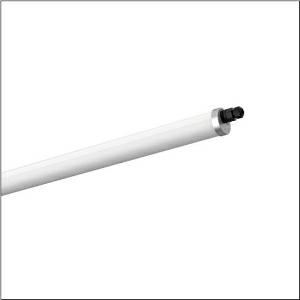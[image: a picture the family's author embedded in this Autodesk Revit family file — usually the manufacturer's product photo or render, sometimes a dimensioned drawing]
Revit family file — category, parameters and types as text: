
# Revit family: monsun_r__31_tube_51ft10dn4a0a_ff33
name_source: partatom
category: Lighting Fixtures
units: mm (PartAtom-declared; Revit-internal decimal feet)

## family parameters
Cut with Voids When Loaded = No
Host = Face
Light Source = No
Part Type = Normal
Room Calculation Point = No
Round Connector Dimension = Use Diameter
Shared = No

## types (1)
- Monsun® 31 Tube (1 x LED, 10000 lm, 58 W, 4000K)
    Apparent Load = 58 VA
    CIE Flux Codes = 42 71 90 91 100
    Color Rendering = 80
    Color Temperature = 4000K
    Default Elevation = 1800 mm
    Description = Monsun® 31 Tube, tubular luminaire, primary optical cover: diffuser, of PMMA, light emission: direct distribution, primary light characteristic: symmetric, installation type: suspended mounting, surface-mounted, LED, rated luminous flux: 10.000lm, luminous efficacy: 160lm/W, light colour: 840, colour temperature: 4000K, control gear: DALI 2, with with 1 terminal, 5-pole, max. 2.5mm², through-wiring: 5x 1.5mm², mains connection: 220..240V, AC, 50/60Hz, rated input power: 58W, housing, cylindrical, of PMMA, semi-transparent, matt white, with luminaire and ceiling fastening, V4A, mounting with brackets of stainless steel, length: 1.570mm, diameter: 75mm, end cap, of stainless steel (V4A), protection rating (complete): IP67/IP69K, insulation class (complete): insulation class I (protective earthing), certification: CE, UKCA, impact resistance: IK07, permissible operating ambient temperature: -20..+40°C, corresponds to IFS (International Featured Standards) requirements for safety and quality in the food industry, usage in unprotected outdoor areas possible with horizontal mounting, contact your sales advisor before using the luminaires in applications with unclear chemical exposure, large temperature fluctuations or condensation-forming humidity, packaging unit: 1 piece
    Height = 83 mm
    Lamp = 1 x LED
    Lamp Light Flux = 10000 lm
    Lamp Power = 58 W
    Lamp count = 1
    Length = 1570 mm
    Luminous efficacy = 172 lm/W
    Manufacturer = Siteco
    ModVariant = No
    Model = 51FT10DN4A0A
    Mounting Place = Ceiling
    Mounting Type = Pendant
    Number of Poles = 1
    OnlyDefault = Yes
    Power Factor = 1
    Product Name = Monsun® 31 Tube
    Product group = tubular luminaire
    ProductGroupID = 906
    Protection Class = Protection class I
    RLX_Detail_Level = 1
    RLX_Emergency_Light_Flux = 0 lm
    RLX_Emergency_Type = 0
    RLX_Emergency_Type_DB = No
    RlxData = <blob elided: 25405 chars, md5=2afcf33a>
    Socket = socket
    Standby Power = 0 W
    System Light Flux = 10000 lm
    System Power = 58 W
    Type Comments = Product without accessories
    Type Image = l_1228461.jpg
    URL = http://relux.com
    VarID = ---
    Voltage = 0 V
    Weight = 0.00 kg
    Width = 75 mm

## geometry (parser evidence)
native form markers: Blend x4, Sweep x12
no freeform markers — native parametric forms only
